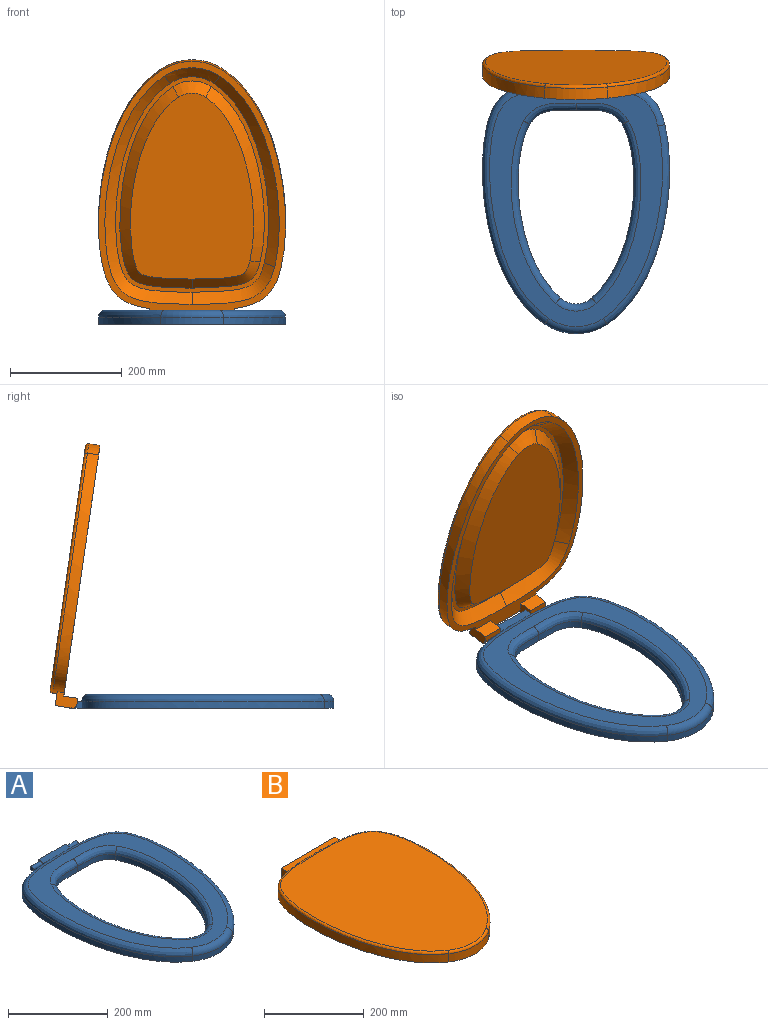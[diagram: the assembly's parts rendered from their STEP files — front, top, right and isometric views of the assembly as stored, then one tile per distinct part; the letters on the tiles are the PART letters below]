
ASSEMBLY  parts=2 mates=1
PART A: 28 faces, bbox 362.2x513.4x25.4 mm
  f0: extruded ~120.65x75.49mm, area 1994.7mm2, adj f5,f10,f17,f22
  f1: extruded ~82.55x25.5mm, area 1161.9mm2, adj f2,f8,f10,f15
  f2: extruded ~310.32x75.49mm, area 4230.1mm2, adj f1,f3,f10,f14
  f3: cylinder r=42.02mm len=55.99mm, axis (0,0,-1), area 778.3mm2, adj f2,f4,f10,f12
  f4: extruded ~310.32x75.49mm, area 4230.1mm2, adj f3,f8,f10,f11
  f5: extruded ~357.04x111.42mm, area 4957.8mm2, adj f0,f7,f10,f16
  f6: extruded ~432.52x129.19mm, area 6951.9mm2, adj f7,f10,f19,f20
  f7: cylinder r=100.11mm len=111.85mm, axis (0,0,-1), area 1507.1mm2, adj f5,f6,f10,f18
  f8: extruded ~82.55x25.5mm, area 1161.9mm2, adj f1,f4,f10,f13
  f9: plane 424.94x309.32mm, normal (0,0,1), area 37972mm2, adj f11,f12,f13,f14,f15,f16,f17,f18
  f10: plane 471.9x362.24mm, normal (0,0,-1), area 67581.1mm2, adj f0,f1,f2,f3,f4,f5,f6,f7
  f11: bspline ~418.88x133.61mm, area 6772.6mm2, adj f4,f9,f12,f13
  f12: torus R=54.72mm, axis (0,0,1), area 1356.7mm2, adj f3,f9,f11,f14
  f13: bspline ~108.46x60.26mm, area 1919.8mm2, adj f8,f9,f11,f15
  f14: bspline ~418.88x133.59mm, area 6772.5mm2, adj f2,f9,f12,f15
  f15: bspline ~108.46x60.23mm, area 1919.8mm2, adj f1,f9,f13,f14
  f16: bspline ~469.98x179.82mm, area 7675mm2, adj f5,f9,f17,f18
  f17: bspline ~170.15x92.02mm, area 3771.3mm2, adj f0,f9,f16,f19,f21
  f18: torus R=87.41mm, axis (0,0,1), area 2258.3mm2, adj f7,f9,f16,f19
  f19: bspline ~491.8x205.47mm, area 11446.9mm2, adj f6,f9,f17,f18,f21
  f20: plane 22.3x12.7mm, normal (-1,0,0), area 212mm2, adj f6,f10,f21,f23,f24
  f21: plane 76.21x22.31mm, normal (0,0,1), area 1663.8mm2, adj f17,f19,f20,f22,f23
  f22: plane 22.3x12.7mm, normal (1,0,0), area 212mm2, adj f0,f10,f21,f23,f26
  f23: plane 76.2x12.7mm, normal (0,1,0), area 967.7mm2, adj f10,f20,f21,f22
  f24: cylinder r=4.76mm len=25.4mm, axis (1,0,0), area 760.1mm2, adj f20,f25
  f25: plane 9.53x9.53mm, normal (-1,0,0), area 71.3mm2, adj f24
  f26: cylinder r=4.76mm len=25.4mm, axis (-1,0,0), area 760.1mm2, adj f22,f27
  f27: plane 9.53x9.53mm, normal (1,0,0), area 71.3mm2, adj f26
PART B: 36 faces, bbox 386.5x543.3x75.1 mm
  f0: extruded ~158.75x76.2mm, area 2996.3mm2, adj f1,f2,f5,f9,f21,f22
  f1: extruded ~433.24x167.32mm, area 10929.6mm2, adj f0,f3,f5,f7,f20,f21
  f2: extruded ~357.04x111.42mm, area 7932.4mm2, adj f0,f3,f5,f8
  f3: cylinder r=100.11mm len=111.85mm, axis (0,0,-1), area 2411.4mm2, adj f1,f2,f5,f6
  f4: plane 440.18x324.56mm, normal (0,0,1), area 117395.8mm2, adj f6,f7,f8,f9
  f5: plane 474.23x364.57mm, normal (0,0,-1), area 16264.6mm2, adj f0,f1,f2,f3,f12,f13,f14,f15
  f6: torus R=95.03mm, axis (0,0,1), area 929.5mm2, adj f3,f4,f7,f8
  f7: bspline ~497.72x233.9mm, area 4635.3mm2, adj f1,f4,f6,f9
  f8: bspline ~440.6x129.87mm, area 3097.1mm2, adj f2,f4,f6,f9
  f9: bspline ~182.98x133.24mm, area 1537.9mm2, adj f0,f4,f7,f8
  f10: plane 413.64x298.28mm, normal (0,0,-1), area 8183.8mm2, adj f12,f13,f14,f15,f16,f17,f18,f19
  f11: plane 338.45x223.41mm, normal (0,0,-1), area 60596mm2, adj f16,f17,f18,f19
  f12: cone r=69.63mm half-angle=45deg, axis (0,0,-1), area 2527.9mm2, adj f5,f10,f13,f14
  f13: bspline ~412.34x159.5mm, area 14335.2mm2, adj f5,f10,f12,f15
  f14: bspline ~344.78x117.09mm, area 9826.4mm2, adj f5,f10,f12,f15
  f15: bspline ~147.75x72.17mm, area 4509.9mm2, adj f5,f10,f13,f14
  f16: cone r=42.96mm half-angle=45deg, axis (0,0,1), area 1676.2mm2, adj f10,f11,f17,f18
  f17: bspline ~363.55x132.18mm, area 12505.3mm2, adj f10,f11,f16,f19
  f18: bspline ~316.19x105.3mm, area 8947.8mm2, adj f10,f11,f16,f19
  f19: bspline ~127.82x51.99mm, area 3556.9mm2, adj f10,f11,f17,f18
  f20: plane 38.1x25.44mm, normal (-1,0,0), area 794.5mm2, adj f1,f5,f21,f23,f24,f26,f35
  f21: plane 153.79x26.14mm, normal (0,0,1), area 3458.7mm2, adj f0,f1,f20,f22,f23
  f22: plane 38.1x25.44mm, normal (1,0,0), area 794.5mm2, adj f0,f5,f21,f23,f28,f29,f34
  f23: plane 152.4x30.48mm, normal (0,1,0), area 3290.3mm2, adj f5,f20,f21,f22,f25,f27,f34,f35
  f24: plane 38.1x25.4mm, normal (0,-1,0), area 967.7mm2, adj f5,f20,f25,f26
  f25: plane 25.4x19.05mm, normal (1,0,0), area 400.2mm2, adj f5,f23,f24,f26,f30,f35
  f26: plane 38.1x11.43mm, normal (0,0,-1), area 435.5mm2, adj f20,f24,f25,f35
  f27: plane 25.4x19.05mm, normal (-1,0,0), area 400.2mm2, adj f5,f23,f28,f29,f32,f34
  f28: plane 38.1x25.4mm, normal (0,-1,0), area 967.7mm2, adj f5,f22,f27,f29
  f29: plane 38.1x11.43mm, normal (0,0,-1), area 435.5mm2, adj f22,f27,f28,f34
  f30: cylinder r=4.76mm len=25.4mm, axis (1,0,0), area 760.1mm2, adj f25,f31
  f31: plane 9.53x9.53mm, normal (1,0,0), area 71.3mm2, adj f30
  f32: cylinder r=4.76mm len=25.4mm, axis (-1,0,0), area 760.1mm2, adj f27,f33
  f33: plane 9.53x9.53mm, normal (-1,0,0), area 71.3mm2, adj f32
  f34: cylinder r=7.62mm len=38.1mm, axis (1,0,0), area 456mm2, adj f22,f23,f27,f29
  f35: cylinder r=7.62mm len=38.1mm, axis (1,0,0), area 456mm2, adj f20,f23,f25,f26
PLACE A t=(73.69,59.69,33.31)mm fixed
PLACE B rot(axis=(-1,0,0),81.8deg) t=(73.69,156.9,132.89)mm
MATE revolute A.f24 <-> B.f30  axis (-1,0,0) through (10.19,151.13,39.66)mm
